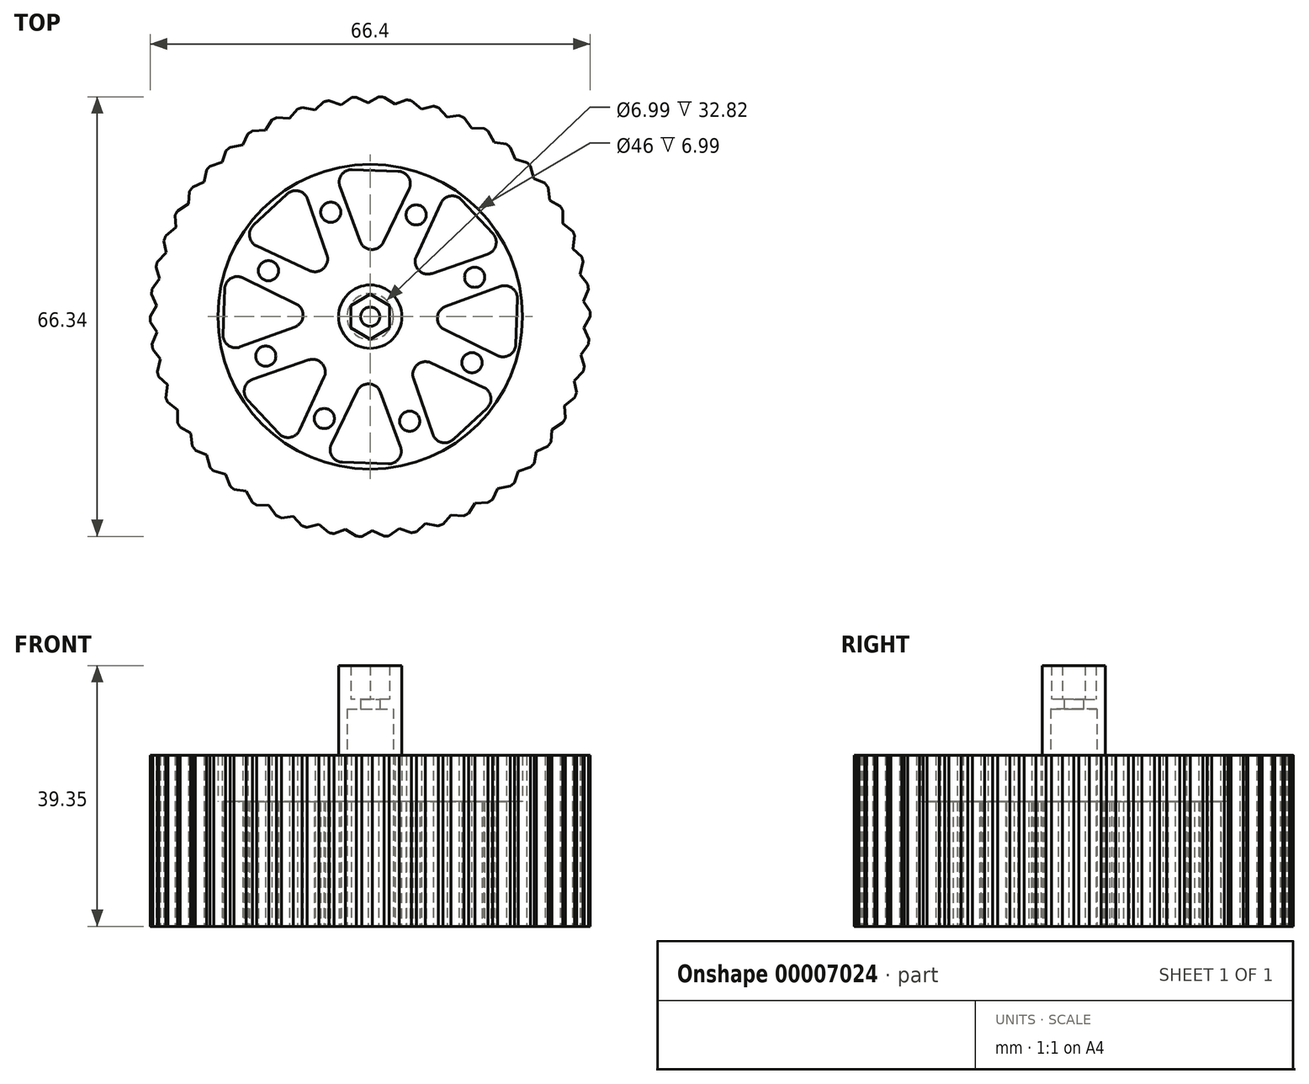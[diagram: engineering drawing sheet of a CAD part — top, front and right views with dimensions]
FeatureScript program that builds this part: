
annotation { "Feature Type Name" : "Feature", "Feature Type Description" : "" }
export const myFeature = defineFeature(function(context is Context, id is Id, definition is map)
    precondition{}
    {
        {
            var Q0;
            Q0=qCreatedBy(makeId("Top.planeOp"),FACE);
            var sketch = newSketch(context, id + "F0", { "sketchPlane" : qUnion([Q0])});
            skCircle(sketch, "E0", {"center": v(0, 0) * mm, "radius": 23 * mm});
            skSolve(sketch);
        }
        {
            var Q0;
            Q0 = qSketchRegion(id + "F0", true);
            extrude(context, id + "F1", {"entities" : qUnion([Q0]), "depth" : 3.8 * mm});
        }
        {
            var Q0;
            Q0=makeQuery(id+"F1.opExtrude","CAP_FACE",FACE,{"disambiguationData":[OSD([sQuery(id+"F0.wireOp",EDGE,"E0")])],"isStart":true});
            var sketch = newSketch(context, id + "F2", { "sketchPlane" : qUnion([Q0])});
            skLineSegment(sketch, "E1.0", {"start": v(4.22, -21.97) * mm, "end": v(-2.71, -22.22) * mm});
            skLineSegment(sketch, "E1.1", {"start": v(-4.57, -19.66) * mm, "end": v(-1.54, -11.39) * mm});
            skLineSegment(sketch, "E1.2", {"start": v(1.96, -11.2) * mm, "end": v(5.87, -19.23) * mm});
            skPoint(sketch, "E1.0.midPoint", {"position": v(0.8, -22.1) * mm});
            skLineSegment(sketch, "E2.1.0", {"start": v(10.67, -17.13) * mm, "end": v(6.96, -9.14) * mm});
            skLineSegment(sketch, "E2.1.1", {"start": v(9.31, -6.54) * mm, "end": v(17.75, -9.45) * mm});
            skLineSegment(sketch, "E2.1.2", {"start": v(18.52, -12.55) * mm, "end": v(13.8, -17.63) * mm});
            skLineSegment(sketch, "E2.2.0", {"start": v(19.66, -4.57) * mm, "end": v(11.39, -1.54) * mm});
            skLineSegment(sketch, "E2.2.1", {"start": v(11.2, 1.96) * mm, "end": v(19.23, 5.87) * mm});
            skLineSegment(sketch, "E2.2.2", {"start": v(21.97, 4.22) * mm, "end": v(22.22, -2.71) * mm});
            skLineSegment(sketch, "E2.3.0", {"start": v(17.13, 10.67) * mm, "end": v(9.14, 6.96) * mm});
            skLineSegment(sketch, "E2.3.1", {"start": v(6.54, 9.31) * mm, "end": v(9.45, 17.75) * mm});
            skLineSegment(sketch, "E2.3.2", {"start": v(12.55, 18.52) * mm, "end": v(17.63, 13.8) * mm});
            skLineSegment(sketch, "E2.4.0", {"start": v(4.57, 19.66) * mm, "end": v(1.54, 11.39) * mm});
            skLineSegment(sketch, "E2.4.1", {"start": v(-1.96, 11.2) * mm, "end": v(-5.87, 19.23) * mm});
            skLineSegment(sketch, "E2.4.2", {"start": v(-4.22, 21.97) * mm, "end": v(2.71, 22.22) * mm});
            skLineSegment(sketch, "E2.5.0", {"start": v(-10.67, 17.13) * mm, "end": v(-6.96, 9.14) * mm});
            skLineSegment(sketch, "E2.5.1", {"start": v(-9.31, 6.54) * mm, "end": v(-17.75, 9.45) * mm});
            skLineSegment(sketch, "E2.5.2", {"start": v(-18.52, 12.55) * mm, "end": v(-13.8, 17.63) * mm});
            skLineSegment(sketch, "E2.6.0", {"start": v(-19.66, 4.57) * mm, "end": v(-11.39, 1.54) * mm});
            skLineSegment(sketch, "E2.6.1", {"start": v(-11.2, -1.96) * mm, "end": v(-19.23, -5.87) * mm});
            skLineSegment(sketch, "E2.6.2", {"start": v(-21.97, -4.22) * mm, "end": v(-22.22, 2.71) * mm});
            skLineSegment(sketch, "E2.7.0", {"start": v(-17.13, -10.67) * mm, "end": v(-9.14, -6.96) * mm});
            skLineSegment(sketch, "E2.7.1", {"start": v(-6.54, -9.31) * mm, "end": v(-9.45, -17.75) * mm});
            skLineSegment(sketch, "E2.7.2", {"start": v(-12.55, -18.52) * mm, "end": v(-17.63, -13.8) * mm});
            skPoint(sketch, "E2.center", {"position": v(0, 0) * mm});
            skLineSegment(sketch, "E3", {"start": v(0.8, -22.1) * mm, "end": v(0, -7.18) * mm, "construction": true});
            skLineSegment(sketch, "E4", {"start": v(-11.86, 19.7) * mm, "end": v(-7.15, 21.86) * mm, "construction": true});
            skLineSegment(sketch, "E5", {"start": v(0, 7.18) * mm, "end": v(0, 0) * mm, "construction": true});
            skLineSegment(sketch, "E6", {"start": v(-7.18, 0) * mm, "end": v(7.18, 0) * mm, "construction": true});
            skPoint(sketch, "E7.visualSharp", {"position": v(-19.7, -11.86) * mm});
            skArc(sketch, "E7.filletArc", {"start": v(-17.13, -10.67) * mm, "mid": v(-18.21, -12.1) * mm, "end": v(-17.63, -13.8) * mm});
            skPoint(sketch, "E8.visualSharp", {"position": v(-10.4, -20.51) * mm});
            skArc(sketch, "E8.filletArc", {"start": v(-12.55, -18.52) * mm, "mid": v(-10.79, -18.97) * mm, "end": v(-9.45, -17.75) * mm});
            skPoint(sketch, "E9.visualSharp", {"position": v(-5.08, -5.08) * mm});
            skArc(sketch, "E9.filletArc", {"start": v(-6.54, -9.31) * mm, "mid": v(-7.06, -7.28) * mm, "end": v(-9.14, -6.96) * mm});
            skPoint(sketch, "E10.visualSharp", {"position": v(-7.18, 0) * mm});
            skArc(sketch, "E10.filletArc", {"start": v(-11.2, -1.96) * mm, "mid": v(-10.14, -0.15) * mm, "end": v(-11.39, 1.54) * mm});
            skPoint(sketch, "E11.visualSharp", {"position": v(-22.32, 5.55) * mm});
            skArc(sketch, "E11.filletArc", {"start": v(-19.66, 4.57) * mm, "mid": v(-21.43, 4.32) * mm, "end": v(-22.22, 2.71) * mm});
            skPoint(sketch, "E12.visualSharp", {"position": v(-21.86, -7.15) * mm});
            skArc(sketch, "E12.filletArc", {"start": v(-21.97, -4.22) * mm, "mid": v(-21.04, -5.79) * mm, "end": v(-19.23, -5.87) * mm});
            skPoint(sketch, "E13.visualSharp", {"position": v(-20.51, 10.4) * mm});
            skArc(sketch, "E13.filletArc", {"start": v(-18.52, 12.55) * mm, "mid": v(-18.97, 10.79) * mm, "end": v(-17.75, 9.45) * mm});
            skPoint(sketch, "E14.visualSharp", {"position": v(-11.86, 19.7) * mm});
            skArc(sketch, "E14.filletArc", {"start": v(-10.67, 17.13) * mm, "mid": v(-12.1, 18.21) * mm, "end": v(-13.8, 17.63) * mm});
            skPoint(sketch, "E15.visualSharp", {"position": v(-5.08, 5.08) * mm});
            skArc(sketch, "E15.filletArc", {"start": v(-9.31, 6.54) * mm, "mid": v(-7.28, 7.06) * mm, "end": v(-6.96, 9.14) * mm});
            skPoint(sketch, "E16.visualSharp", {"position": v(0, 7.18) * mm});
            skArc(sketch, "E16.filletArc", {"start": v(-1.96, 11.2) * mm, "mid": v(-0.15, 10.14) * mm, "end": v(1.54, 11.39) * mm});
            skPoint(sketch, "E17.visualSharp", {"position": v(-7.15, 21.86) * mm});
            skArc(sketch, "E17.filletArc", {"start": v(-4.22, 21.97) * mm, "mid": v(-5.79, 21.04) * mm, "end": v(-5.87, 19.23) * mm});
            skPoint(sketch, "E18.visualSharp", {"position": v(5.55, 22.32) * mm});
            skArc(sketch, "E18.filletArc", {"start": v(4.57, 19.66) * mm, "mid": v(4.32, 21.43) * mm, "end": v(2.71, 22.22) * mm});
            skPoint(sketch, "E19.visualSharp", {"position": v(5.08, 5.08) * mm});
            skArc(sketch, "E19.filletArc", {"start": v(6.54, 9.31) * mm, "mid": v(7.06, 7.28) * mm, "end": v(9.14, 6.96) * mm});
            skPoint(sketch, "E20.visualSharp", {"position": v(10.4, 20.51) * mm});
            skArc(sketch, "E20.filletArc", {"start": v(12.55, 18.52) * mm, "mid": v(10.79, 18.97) * mm, "end": v(9.45, 17.75) * mm});
            skPoint(sketch, "E21.visualSharp", {"position": v(19.7, 11.86) * mm});
            skArc(sketch, "E21.filletArc", {"start": v(17.13, 10.67) * mm, "mid": v(18.21, 12.1) * mm, "end": v(17.63, 13.8) * mm});
            skPoint(sketch, "E22.visualSharp", {"position": v(21.86, 7.15) * mm});
            skArc(sketch, "E22.filletArc", {"start": v(21.97, 4.22) * mm, "mid": v(21.04, 5.79) * mm, "end": v(19.23, 5.87) * mm});
            skPoint(sketch, "E23.visualSharp", {"position": v(7.18, 0) * mm});
            skArc(sketch, "E23.filletArc", {"start": v(11.2, 1.96) * mm, "mid": v(10.14, 0.15) * mm, "end": v(11.39, -1.54) * mm});
            skPoint(sketch, "E24.visualSharp", {"position": v(22.32, -5.55) * mm});
            skArc(sketch, "E24.filletArc", {"start": v(19.66, -4.57) * mm, "mid": v(21.43, -4.32) * mm, "end": v(22.22, -2.71) * mm});
            skPoint(sketch, "E25.visualSharp", {"position": v(11.86, -19.7) * mm});
            skArc(sketch, "E25.filletArc", {"start": v(10.67, -17.13) * mm, "mid": v(12.1, -18.21) * mm, "end": v(13.8, -17.63) * mm});
            skPoint(sketch, "E26.visualSharp", {"position": v(5.08, -5.08) * mm});
            skArc(sketch, "E26.filletArc", {"start": v(9.31, -6.54) * mm, "mid": v(7.28, -7.06) * mm, "end": v(6.96, -9.14) * mm});
            skPoint(sketch, "E27.visualSharp", {"position": v(20.51, -10.4) * mm});
            skArc(sketch, "E27.filletArc", {"start": v(18.52, -12.55) * mm, "mid": v(18.97, -10.79) * mm, "end": v(17.75, -9.45) * mm});
            skPoint(sketch, "E28.visualSharp", {"position": v(0, -7.18) * mm});
            skArc(sketch, "E28.filletArc", {"start": v(1.96, -11.2) * mm, "mid": v(0.15, -10.14) * mm, "end": v(-1.54, -11.39) * mm});
            skPoint(sketch, "E29.visualSharp", {"position": v(-5.55, -22.32) * mm});
            skArc(sketch, "E29.filletArc", {"start": v(-4.57, -19.66) * mm, "mid": v(-4.32, -21.43) * mm, "end": v(-2.71, -22.22) * mm});
            skPoint(sketch, "E30.visualSharp", {"position": v(7.15, -21.86) * mm});
            skArc(sketch, "E30.filletArc", {"start": v(4.22, -21.97) * mm, "mid": v(5.79, -21.04) * mm, "end": v(5.87, -19.23) * mm});
            skSolve(sketch);
        }
        {
            var Q0;
            {var subQ11=sQuery(id+"F2.wireOp",EDGE,"E1.1");Q0=makeQuery(id+"F2.imprint","IMPRINT",FACE,{"disambiguationData":[TD([[makeQuery(id+"F2.imprint","IMPRINT",EDGE,{"derivedFrom":subQ11}),1.0]])]});}
            var sketch = newSketch(context, id + "F3", { "sketchPlane" : qUnion([Q0])});
            skCircle(sketch, "E31", {"center": v(0, 0) * mm, "radius": 4.79 * mm});
            skSolve(sketch);
        }
        {
            var Q0;
            Q0 = qSketchRegion(id + "F3", true);
            extrude(context, id + "F4", {"entities" : qUnion([Q0]), "operationType" : NewBodyOperationType.ADD, "oppositeDirection" : true, "depth" : 14.55 * mm});
        }
        {
            var Q0;
            Q0=makeQuery(id+"F3.imprint","IMPRINT",FACE,{"disambiguationData":[TD([[makeQuery(id+"F3.imprint","IMPRINT",EDGE,{"derivedFrom":sQuery(id+"F3.wireOp",EDGE,"E31")}),1.0]])]});
            var sketch = newSketch(context, id + "F5", { "sketchPlane" : qUnion([Q0])});
            skCircle(sketch, "E32", {"center": v(0, 0) * mm, "radius": 3.5 * mm});
            skSolve(sketch);
        }
        {
            var Q0;
            Q0 = qSketchRegion(id + "F5", true);
            extrude(context, id + "F6", {"entities" : qUnion([Q0]), "operationType" : NewBodyOperationType.REMOVE, "oppositeDirection" : true, "depth" : 7.62 * mm});
        }
        {
            var Q0;
            Q0=makeQuery(id+"F4.opExtrude","CAP_FACE",FACE,{"disambiguationData":[OSD([sQuery(id+"F3.wireOp",EDGE,"E31")])],"isStart":false});
            var sketch = newSketch(context, id + "F7", { "sketchPlane" : qUnion([Q0])});
            skCircle(sketch, "E33.cCircle", {"center": v(0, 0) * mm, "radius": 2.93 * mm, "construction": true});
            skLineSegment(sketch, "E33.0", {"start": v(2.93, 1.69) * mm, "end": v(2.93, -1.69) * mm});
            skLineSegment(sketch, "E33.1", {"start": v(2.93, -1.69) * mm, "end": v(0, -3.38) * mm});
            skLineSegment(sketch, "E33.2", {"start": v(0, -3.38) * mm, "end": v(-2.93, -1.69) * mm});
            skLineSegment(sketch, "E33.3", {"start": v(-2.93, -1.69) * mm, "end": v(-2.93, 1.69) * mm});
            skLineSegment(sketch, "E33.4", {"start": v(-2.93, 1.69) * mm, "end": v(0, 3.38) * mm});
            skLineSegment(sketch, "E33.5", {"start": v(0, 3.38) * mm, "end": v(2.93, 1.69) * mm});
            skPoint(sketch, "E33.0.midPoint", {"position": v(2.93, 0) * mm});
            skSolve(sketch);
        }
        {
            var Q0;
            Q0=makeQuery(id+"F7.imprint","IMPRINT",FACE,{"disambiguationData":[TD([[makeQuery(id+"F7.imprint","IMPRINT",EDGE,{"derivedFrom":sQuery(id+"F7.wireOp",EDGE,"E33.0")}),-1.0]])]});
            extrude(context, id + "F8", {"entities" : qUnion([Q0]), "operationType" : NewBodyOperationType.REMOVE, "oppositeDirection" : true, "depth" : 5.08 * mm});
        }
        {
            var Q0;
            {var subQ11=sQuery(id+"F2.wireOp",EDGE,"E1.1");Q0=makeQuery(id+"F2.imprint","IMPRINT",FACE,{"disambiguationData":[TD([[makeQuery(id+"F2.imprint","IMPRINT",EDGE,{"derivedFrom":subQ11}),1.0]])]});}
            var sketch = newSketch(context, id + "F9", { "sketchPlane" : qUnion([Q0])});
            skCircle(sketch, "E34", {"center": v(0, 0) * mm, "radius": 1.45 * mm});
            skSolve(sketch);
        }
        {
            var Q0;
            Q0 = qSketchRegion(id + "F9", true);
            extrude(context, id + "F10", {"entities" : qUnion([Q0]), "operationType" : NewBodyOperationType.REMOVE, "oppositeDirection" : true, "depth" : 25.4 * mm});
        }
        {
            var Q0;
            {var subQ11=sQuery(id+"F2.wireOp",EDGE,"E1.1");Q0=makeQuery(id+"F2.imprint","IMPRINT",FACE,{"disambiguationData":[TD([[makeQuery(id+"F2.imprint","IMPRINT",EDGE,{"derivedFrom":subQ11}),1.0]])]});}
            var sketch = newSketch(context, id + "F11", { "sketchPlane" : qUnion([Q0])});
            skLineSegment(sketch, "E35", {"start": v(8.77, 15.77) * mm, "end": v(3.15, 15.77) * mm, "construction": true});
            skCircle(sketch, "E36", {"center": v(5.96, 15.77) * mm, "radius": 1.52 * mm});
            skCircle(sketch, "E37.1.0", {"center": v(-6.94, 15.37) * mm, "radius": 1.52 * mm});
            skCircle(sketch, "E37.2.0", {"center": v(-15.77, 5.96) * mm, "radius": 1.52 * mm});
            skCircle(sketch, "E37.3.0", {"center": v(-15.37, -6.94) * mm, "radius": 1.52 * mm});
            skCircle(sketch, "E37.4.0", {"center": v(-5.96, -15.77) * mm, "radius": 1.52 * mm});
            skCircle(sketch, "E37.5.0", {"center": v(6.94, -15.37) * mm, "radius": 1.52 * mm});
            skCircle(sketch, "E37.6.0", {"center": v(15.77, -5.96) * mm, "radius": 1.52 * mm});
            skCircle(sketch, "E37.7.0", {"center": v(15.37, 6.94) * mm, "radius": 1.52 * mm});
            skPoint(sketch, "E37.center", {"position": v(0, 0) * mm});
            skSolve(sketch);
        }
        {
            var Q0;
            Q0 = qSketchRegion(id + "F11", true);
            extrude(context, id + "F12", {"entities" : qUnion([Q0]), "operationType" : NewBodyOperationType.REMOVE, "oppositeDirection" : true, "depth" : 12.7 * mm});
        }
        {
            var Q0;
            Q0=makeQuery(id+"F3.imprint","IMPRINT",FACE,{"disambiguationData":[TD([[makeQuery(id+"F3.imprint","IMPRINT",EDGE,{"derivedFrom":sQuery(id+"F3.wireOp",EDGE,"E31")}),-1.0]])]});
            var sketch = newSketch(context, id + "F13", { "sketchPlane" : qUnion([Q0])});
            skCircle(sketch, "E38", {"center": v(0, 0) * mm, "radius": 33.2 * mm});
            skCircle(sketch, "E39", {"center": v(0, 0) * mm, "radius": 21.9 * mm});
            skCircle(sketch, "E40.0", {"center": v(0, 0) * mm, "radius": 23 * mm});
            skSolve(sketch);
        }
        {
            var Q0;
            Q0 = qSketchRegion(id + "F2", true);
            extrude(context, id + "F14", {"entities" : qUnion([Q0]), "operationType" : NewBodyOperationType.REMOVE, "oppositeDirection" : true, "depth" : 12.7 * mm, "offsetDistance" : 25 * mm});
        }
        {
            var Q0;
            Q0=makeQuery(id+"F13.imprint","IMPRINT",FACE,{"disambiguationData":[TD([[makeQuery(id+"F13.imprint","IMPRINT",EDGE,{"derivedFrom":sQuery(id+"F13.wireOp",EDGE,"E38")}),1.0]])]});
            extrude(context, id + "F15", {"entities" : qUnion([Q0]), "operationType" : NewBodyOperationType.ADD, "oppositeDirection" : true, "depth" : 18 * mm, "offsetDistance" : 25 * mm});
        }
        {
            var Q0;
            Q0=makeQuery(id+"F4.opExtrude","CAP_FACE",FACE,{"disambiguationData":[OSD([sQuery(id+"F3.wireOp",EDGE,"E31")])],"isStart":false});
            extrude(context, id + "F16", {"entities" : qUnion([Q0]), "operationType" : NewBodyOperationType.ADD, "depth" : 17 * mm, "offsetDistance" : 25 * mm});
        }
        {
            var Q0;
            Q0=makeQuery(id+"F8.boolean.opBoolean","COPY",FACE,{"derivedFrom":makeQuery(id+"F8.opExtrude","CAP_FACE",FACE,{"disambiguationData":[OSD([sQuery(id+"F7.wireOp",EDGE,"E33.0"),sQuery(id+"F7.wireOp",EDGE,"E33.1"),sQuery(id+"F7.wireOp",EDGE,"E33.2"),sQuery(id+"F7.wireOp",EDGE,"E33.3"),sQuery(id+"F7.wireOp",EDGE,"E33.4"),sQuery(id+"F7.wireOp",EDGE,"E33.5")])],"isStart":false})});
            extrude(context, id + "F17", {"entities" : qUnion([Q0]), "operationType" : NewBodyOperationType.ADD, "depth" : 17 * mm, "offsetDistance" : 25 * mm});
        }
        {
            var Q0;
            Q0=makeQuery(id+"F6.boolean.opBoolean","COPY",FACE,{"derivedFrom":makeQuery(id+"F6.opExtrude","CAP_FACE",FACE,{"disambiguationData":[OSD([sQuery(id+"F5.wireOp",EDGE,"E32")])],"isStart":false})});
            extrude(context, id + "F18", {"entities" : qUnion([Q0]), "operationType" : NewBodyOperationType.REMOVE, "oppositeDirection" : true, "depth" : 17.4 * mm, "offsetDistance" : 25 * mm});
        }
        {
            var Q0;
            Q0=makeQuery(id+"F1.opExtrude","CAP_FACE",FACE,{"disambiguationData":[OSD([sQuery(id+"F0.wireOp",EDGE,"E0")])],"isStart":false});
            extrude(context, id + "F19", {"entities" : qUnion([Q0]), "operationType" : NewBodyOperationType.ADD, "depth" : 11.5 * mm, "offsetDistance" : 25 * mm});
        }
        {
            var Q0;
            Q0=makeQuery(id+"F15.boolean.opBoolean","MERGE",FACE,{"derivedFrom":[makeQuery(id+"F1.opExtrude","CAP_FACE",FACE,{"disambiguationData":[OSD([sQuery(id+"F0.wireOp",EDGE,"E0")])],"isStart":true}),makeQuery(id+"F15.opExtrude","CAP_FACE",FACE,{"disambiguationData":[OSD([sQuery(id+"F13.wireOp",EDGE,"E38"),sQuery(id+"F13.wireOp",EDGE,"E40.0")])],"isStart":true})]});
            var sketch = newSketch(context, id + "F20", { "sketchPlane" : qUnion([Q0])});
            skLineSegment(sketch, "E41", {"start": v(33.03, 3.38) * mm, "end": v(32.25, 1.7) * mm});
            skLineSegment(sketch, "E42", {"start": v(32.25, 1.7) * mm, "end": v(33.2, 0) * mm});
            skArc(sketch, "E43.0", {"start": v(33.2, 0) * mm, "mid": v(33.16, 1.7) * mm, "end": v(33.03, 3.38) * mm});
            skLineSegment(sketch, "E44.1.0", {"start": v(31.78, 5.74) * mm, "end": v(32.94, 4.16) * mm});
            skLineSegment(sketch, "E44.1.1", {"start": v(32.34, 7.49) * mm, "end": v(31.78, 5.74) * mm});
            skArc(sketch, "E44.1.2", {"start": v(32.94, 4.16) * mm, "mid": v(32.68, 5.83) * mm, "end": v(32.34, 7.49) * mm});
            skLineSegment(sketch, "E44.2.0", {"start": v(30.81, 9.68) * mm, "end": v(32.16, 8.26) * mm});
            skLineSegment(sketch, "E44.2.1", {"start": v(31.15, 11.48) * mm, "end": v(30.81, 9.68) * mm});
            skArc(sketch, "E44.2.2", {"start": v(32.16, 8.26) * mm, "mid": v(31.7, 9.88) * mm, "end": v(31.15, 11.48) * mm});
            skLineSegment(sketch, "E44.3.0", {"start": v(29.36, 13.46) * mm, "end": v(30.87, 12.22) * mm});
            skLineSegment(sketch, "E44.3.1", {"start": v(29.47, 15.3) * mm, "end": v(29.36, 13.46) * mm});
            skArc(sketch, "E44.3.2", {"start": v(30.87, 12.22) * mm, "mid": v(30.2, 13.78) * mm, "end": v(29.47, 15.3) * mm});
            skLineSegment(sketch, "E44.4.0", {"start": v(27.44, 17.04) * mm, "end": v(29.1, 16) * mm});
            skLineSegment(sketch, "E44.4.1", {"start": v(27.32, 18.87) * mm, "end": v(27.44, 17.04) * mm});
            skArc(sketch, "E44.4.2", {"start": v(29.1, 16) * mm, "mid": v(28.24, 17.45) * mm, "end": v(27.32, 18.87) * mm});
            skLineSegment(sketch, "E44.5.0", {"start": v(25.09, 20.34) * mm, "end": v(26.86, 19.51) * mm});
            skLineSegment(sketch, "E44.5.1", {"start": v(24.73, 22.15) * mm, "end": v(25.09, 20.34) * mm});
            skArc(sketch, "E44.5.2", {"start": v(26.86, 19.51) * mm, "mid": v(25.83, 20.86) * mm, "end": v(24.73, 22.15) * mm});
            skLineSegment(sketch, "E44.6.0", {"start": v(22.34, 23.32) * mm, "end": v(24.2, 22.73) * mm});
            skLineSegment(sketch, "E44.6.1", {"start": v(21.76, 25.07) * mm, "end": v(22.34, 23.32) * mm});
            skArc(sketch, "E44.6.2", {"start": v(24.2, 22.73) * mm, "mid": v(23.01, 23.93) * mm, "end": v(21.76, 25.07) * mm});
            skLineSegment(sketch, "E44.7.0", {"start": v(19.24, 25.94) * mm, "end": v(21.16, 25.58) * mm});
            skLineSegment(sketch, "E44.7.1", {"start": v(18.45, 27.6) * mm, "end": v(19.24, 25.94) * mm});
            skArc(sketch, "E44.7.2", {"start": v(21.16, 25.58) * mm, "mid": v(19.83, 26.63) * mm, "end": v(18.45, 27.6) * mm});
            skLineSegment(sketch, "E44.8.0", {"start": v(15.84, 28.15) * mm, "end": v(17.79, 28.03) * mm});
            skLineSegment(sketch, "E44.8.1", {"start": v(14.85, 29.7) * mm, "end": v(15.84, 28.15) * mm});
            skArc(sketch, "E44.8.2", {"start": v(17.79, 28.03) * mm, "mid": v(16.34, 28.9) * mm, "end": v(14.85, 29.7) * mm});
            skLineSegment(sketch, "E44.9.0", {"start": v(12.19, 29.91) * mm, "end": v(14.14, 30.04) * mm});
            skLineSegment(sketch, "E44.9.1", {"start": v(11, 31.32) * mm, "end": v(12.19, 29.91) * mm});
            skArc(sketch, "E44.9.2", {"start": v(14.14, 30.04) * mm, "mid": v(12.59, 30.72) * mm, "end": v(11, 31.32) * mm});
            skLineSegment(sketch, "E44.10.0", {"start": v(8.34, 31.2) * mm, "end": v(10.26, 31.57) * mm});
            skLineSegment(sketch, "E44.10.1", {"start": v(7, 32.45) * mm, "end": v(8.34, 31.2) * mm});
            skArc(sketch, "E44.10.2", {"start": v(10.26, 31.57) * mm, "mid": v(8.64, 32.06) * mm, "end": v(7, 32.45) * mm});
            skLineSegment(sketch, "E44.11.0", {"start": v(4.36, 32) * mm, "end": v(6.22, 32.61) * mm});
            skLineSegment(sketch, "E44.11.1", {"start": v(2.87, 33.08) * mm, "end": v(4.36, 32) * mm});
            skArc(sketch, "E44.11.2", {"start": v(6.22, 32.61) * mm, "mid": v(4.55, 32.89) * mm, "end": v(2.87, 33.08) * mm});
            skLineSegment(sketch, "E44.12.0", {"start": v(0.32, 32.3) * mm, "end": v(2.08, 33.13) * mm});
            skLineSegment(sketch, "E44.12.1", {"start": v(-1.3, 33.17) * mm, "end": v(0.32, 32.3) * mm});
            skArc(sketch, "E44.12.2", {"start": v(2.08, 33.13) * mm, "mid": v(0.4, 33.2) * mm, "end": v(-1.3, 33.17) * mm});
            skLineSegment(sketch, "E44.13.0", {"start": v(-3.73, 32.08) * mm, "end": v(-2.08, 33.13) * mm});
            skLineSegment(sketch, "E44.13.1", {"start": v(-5.44, 32.75) * mm, "end": v(-3.73, 32.08) * mm});
            skArc(sketch, "E44.13.2", {"start": v(-2.08, 33.13) * mm, "mid": v(-3.77, 32.99) * mm, "end": v(-5.44, 32.75) * mm});
            skLineSegment(sketch, "E44.14.0", {"start": v(-7.72, 31.36) * mm, "end": v(-6.22, 32.61) * mm});
            skLineSegment(sketch, "E44.14.1", {"start": v(-9.5, 31.8) * mm, "end": v(-7.72, 31.36) * mm});
            skArc(sketch, "E44.14.2", {"start": v(-6.22, 32.61) * mm, "mid": v(-7.87, 32.25) * mm, "end": v(-9.5, 31.8) * mm});
            skLineSegment(sketch, "E44.15.0", {"start": v(-11.6, 30.15) * mm, "end": v(-10.26, 31.57) * mm});
            skLineSegment(sketch, "E44.15.1", {"start": v(-13.42, 30.37) * mm, "end": v(-11.6, 30.15) * mm});
            skArc(sketch, "E44.15.2", {"start": v(-10.26, 31.57) * mm, "mid": v(-11.85, 31.01) * mm, "end": v(-13.42, 30.37) * mm});
            skLineSegment(sketch, "E44.16.0", {"start": v(-15.28, 28.46) * mm, "end": v(-14.14, 30.04) * mm});
            skLineSegment(sketch, "E44.16.1", {"start": v(-17.12, 28.45) * mm, "end": v(-15.28, 28.46) * mm});
            skArc(sketch, "E44.16.2", {"start": v(-14.14, 30.04) * mm, "mid": v(-15.65, 29.28) * mm, "end": v(-17.12, 28.45) * mm});
            skLineSegment(sketch, "E44.17.0", {"start": v(-18.72, 26.32) * mm, "end": v(-17.79, 28.03) * mm});
            skLineSegment(sketch, "E44.17.1", {"start": v(-20.55, 26.08) * mm, "end": v(-18.72, 26.32) * mm});
            skArc(sketch, "E44.17.2", {"start": v(-17.79, 28.03) * mm, "mid": v(-19.2, 27.09) * mm, "end": v(-20.55, 26.08) * mm});
            skLineSegment(sketch, "E44.18.0", {"start": v(-21.88, 23.76) * mm, "end": v(-21.16, 25.58) * mm});
            skLineSegment(sketch, "E44.18.1", {"start": v(-23.65, 23.3) * mm, "end": v(-21.88, 23.76) * mm});
            skArc(sketch, "E44.18.2", {"start": v(-21.16, 25.58) * mm, "mid": v(-22.44, 24.47) * mm, "end": v(-23.65, 23.3) * mm});
            skLineSegment(sketch, "E44.19.0", {"start": v(-24.68, 20.83) * mm, "end": v(-24.2, 22.73) * mm});
            skLineSegment(sketch, "E44.19.1", {"start": v(-26.39, 20.15) * mm, "end": v(-24.68, 20.83) * mm});
            skArc(sketch, "E44.19.2", {"start": v(-24.2, 22.73) * mm, "mid": v(-25.33, 21.46) * mm, "end": v(-26.39, 20.15) * mm});
            skLineSegment(sketch, "E44.20.0", {"start": v(-27.1, 17.58) * mm, "end": v(-26.86, 19.51) * mm});
            skLineSegment(sketch, "E44.20.1", {"start": v(-28.7, 16.68) * mm, "end": v(-27.1, 17.58) * mm});
            skArc(sketch, "E44.20.2", {"start": v(-26.86, 19.51) * mm, "mid": v(-27.82, 18.12) * mm, "end": v(-28.7, 16.68) * mm});
            skLineSegment(sketch, "E44.21.0", {"start": v(-29.09, 14.04) * mm, "end": v(-29.1, 16) * mm});
            skLineSegment(sketch, "E44.21.1", {"start": v(-30.57, 12.95) * mm, "end": v(-29.09, 14.04) * mm});
            skArc(sketch, "E44.21.2", {"start": v(-29.1, 16) * mm, "mid": v(-29.87, 14.5) * mm, "end": v(-30.57, 12.95) * mm});
            skLineSegment(sketch, "E44.22.0", {"start": v(-30.62, 10.28) * mm, "end": v(-30.87, 12.22) * mm});
            skLineSegment(sketch, "E44.22.1", {"start": v(-31.95, 9.02) * mm, "end": v(-30.62, 10.28) * mm});
            skArc(sketch, "E44.22.2", {"start": v(-30.87, 12.22) * mm, "mid": v(-31.45, 10.63) * mm, "end": v(-31.95, 9.02) * mm});
            skLineSegment(sketch, "E44.23.0", {"start": v(-31.66, 6.37) * mm, "end": v(-32.16, 8.26) * mm});
            skLineSegment(sketch, "E44.23.1", {"start": v(-32.83, 4.94) * mm, "end": v(-31.66, 6.37) * mm});
            skArc(sketch, "E44.23.2", {"start": v(-32.16, 8.26) * mm, "mid": v(-32.54, 6.6) * mm, "end": v(-32.83, 4.94) * mm});
            skLineSegment(sketch, "E44.24.0", {"start": v(-32.21, 2.35) * mm, "end": v(-32.94, 4.16) * mm});
            skLineSegment(sketch, "E44.24.1", {"start": v(-33.2, 0.79) * mm, "end": v(-32.21, 2.35) * mm});
            skArc(sketch, "E44.24.2", {"start": v(-32.94, 4.16) * mm, "mid": v(-33.1, 2.48) * mm, "end": v(-33.2, 0.79) * mm});
            skLineSegment(sketch, "E44.25.0", {"start": v(-32.25, -1.7) * mm, "end": v(-33.2, 0) * mm});
            skLineSegment(sketch, "E44.25.1", {"start": v(-33.03, -3.38) * mm, "end": v(-32.25, -1.7) * mm});
            skArc(sketch, "E44.25.2", {"start": v(-33.2, 0) * mm, "mid": v(-33.16, -1.7) * mm, "end": v(-33.03, -3.38) * mm});
            skLineSegment(sketch, "E44.26.0", {"start": v(-31.78, -5.74) * mm, "end": v(-32.94, -4.16) * mm});
            skLineSegment(sketch, "E44.26.1", {"start": v(-32.34, -7.49) * mm, "end": v(-31.78, -5.74) * mm});
            skArc(sketch, "E44.26.2", {"start": v(-32.94, -4.16) * mm, "mid": v(-32.68, -5.83) * mm, "end": v(-32.34, -7.49) * mm});
            skLineSegment(sketch, "E44.27.0", {"start": v(-30.81, -9.68) * mm, "end": v(-32.16, -8.26) * mm});
            skLineSegment(sketch, "E44.27.1", {"start": v(-31.15, -11.48) * mm, "end": v(-30.81, -9.68) * mm});
            skArc(sketch, "E44.27.2", {"start": v(-32.16, -8.26) * mm, "mid": v(-31.7, -9.88) * mm, "end": v(-31.15, -11.48) * mm});
            skLineSegment(sketch, "E44.28.0", {"start": v(-29.36, -13.46) * mm, "end": v(-30.87, -12.22) * mm});
            skLineSegment(sketch, "E44.28.1", {"start": v(-29.47, -15.3) * mm, "end": v(-29.36, -13.46) * mm});
            skArc(sketch, "E44.28.2", {"start": v(-30.87, -12.22) * mm, "mid": v(-30.2, -13.78) * mm, "end": v(-29.47, -15.3) * mm});
            skLineSegment(sketch, "E44.29.0", {"start": v(-27.44, -17.04) * mm, "end": v(-29.1, -16) * mm});
            skLineSegment(sketch, "E44.29.1", {"start": v(-27.32, -18.87) * mm, "end": v(-27.44, -17.04) * mm});
            skArc(sketch, "E44.29.2", {"start": v(-29.1, -16) * mm, "mid": v(-28.24, -17.45) * mm, "end": v(-27.32, -18.87) * mm});
            skLineSegment(sketch, "E44.30.0", {"start": v(-25.09, -20.34) * mm, "end": v(-26.86, -19.51) * mm});
            skLineSegment(sketch, "E44.30.1", {"start": v(-24.73, -22.15) * mm, "end": v(-25.09, -20.34) * mm});
            skArc(sketch, "E44.30.2", {"start": v(-26.86, -19.51) * mm, "mid": v(-25.83, -20.86) * mm, "end": v(-24.73, -22.15) * mm});
            skLineSegment(sketch, "E44.31.0", {"start": v(-22.34, -23.32) * mm, "end": v(-24.2, -22.73) * mm});
            skLineSegment(sketch, "E44.31.1", {"start": v(-21.76, -25.07) * mm, "end": v(-22.34, -23.32) * mm});
            skArc(sketch, "E44.31.2", {"start": v(-24.2, -22.73) * mm, "mid": v(-23.01, -23.93) * mm, "end": v(-21.76, -25.07) * mm});
            skLineSegment(sketch, "E44.32.0", {"start": v(-19.24, -25.94) * mm, "end": v(-21.16, -25.58) * mm});
            skLineSegment(sketch, "E44.32.1", {"start": v(-18.45, -27.6) * mm, "end": v(-19.24, -25.94) * mm});
            skArc(sketch, "E44.32.2", {"start": v(-21.16, -25.58) * mm, "mid": v(-19.83, -26.63) * mm, "end": v(-18.45, -27.6) * mm});
            skLineSegment(sketch, "E44.33.0", {"start": v(-15.84, -28.15) * mm, "end": v(-17.79, -28.03) * mm});
            skLineSegment(sketch, "E44.33.1", {"start": v(-14.85, -29.7) * mm, "end": v(-15.84, -28.15) * mm});
            skArc(sketch, "E44.33.2", {"start": v(-17.79, -28.03) * mm, "mid": v(-16.34, -28.9) * mm, "end": v(-14.85, -29.7) * mm});
            skLineSegment(sketch, "E44.34.0", {"start": v(-12.19, -29.91) * mm, "end": v(-14.14, -30.04) * mm});
            skLineSegment(sketch, "E44.34.1", {"start": v(-11, -31.32) * mm, "end": v(-12.19, -29.91) * mm});
            skArc(sketch, "E44.34.2", {"start": v(-14.14, -30.04) * mm, "mid": v(-12.59, -30.72) * mm, "end": v(-11, -31.32) * mm});
            skLineSegment(sketch, "E44.35.0", {"start": v(-8.34, -31.2) * mm, "end": v(-10.26, -31.57) * mm});
            skLineSegment(sketch, "E44.35.1", {"start": v(-7, -32.45) * mm, "end": v(-8.34, -31.2) * mm});
            skArc(sketch, "E44.35.2", {"start": v(-10.26, -31.57) * mm, "mid": v(-8.64, -32.06) * mm, "end": v(-7, -32.45) * mm});
            skLineSegment(sketch, "E44.36.0", {"start": v(-4.36, -32) * mm, "end": v(-6.22, -32.61) * mm});
            skLineSegment(sketch, "E44.36.1", {"start": v(-2.87, -33.08) * mm, "end": v(-4.36, -32) * mm});
            skArc(sketch, "E44.36.2", {"start": v(-6.22, -32.61) * mm, "mid": v(-4.55, -32.89) * mm, "end": v(-2.87, -33.08) * mm});
            skLineSegment(sketch, "E44.37.0", {"start": v(-0.32, -32.3) * mm, "end": v(-2.08, -33.13) * mm});
            skLineSegment(sketch, "E44.37.1", {"start": v(1.3, -33.17) * mm, "end": v(-0.32, -32.3) * mm});
            skArc(sketch, "E44.37.2", {"start": v(-2.08, -33.13) * mm, "mid": v(-0.4, -33.2) * mm, "end": v(1.3, -33.17) * mm});
            skLineSegment(sketch, "E44.38.0", {"start": v(3.73, -32.08) * mm, "end": v(2.08, -33.13) * mm});
            skLineSegment(sketch, "E44.38.1", {"start": v(5.44, -32.75) * mm, "end": v(3.73, -32.08) * mm});
            skArc(sketch, "E44.38.2", {"start": v(2.08, -33.13) * mm, "mid": v(3.77, -32.99) * mm, "end": v(5.44, -32.75) * mm});
            skLineSegment(sketch, "E44.39.0", {"start": v(7.72, -31.36) * mm, "end": v(6.22, -32.61) * mm});
            skLineSegment(sketch, "E44.39.1", {"start": v(9.5, -31.8) * mm, "end": v(7.72, -31.36) * mm});
            skArc(sketch, "E44.39.2", {"start": v(6.22, -32.61) * mm, "mid": v(7.87, -32.25) * mm, "end": v(9.5, -31.8) * mm});
            skLineSegment(sketch, "E44.40.0", {"start": v(11.6, -30.15) * mm, "end": v(10.26, -31.57) * mm});
            skLineSegment(sketch, "E44.40.1", {"start": v(13.42, -30.37) * mm, "end": v(11.6, -30.15) * mm});
            skArc(sketch, "E44.40.2", {"start": v(10.26, -31.57) * mm, "mid": v(11.85, -31.01) * mm, "end": v(13.42, -30.37) * mm});
            skLineSegment(sketch, "E44.41.0", {"start": v(15.28, -28.46) * mm, "end": v(14.14, -30.04) * mm});
            skLineSegment(sketch, "E44.41.1", {"start": v(17.12, -28.45) * mm, "end": v(15.28, -28.46) * mm});
            skArc(sketch, "E44.41.2", {"start": v(14.14, -30.04) * mm, "mid": v(15.65, -29.28) * mm, "end": v(17.12, -28.45) * mm});
            skLineSegment(sketch, "E44.42.0", {"start": v(18.72, -26.32) * mm, "end": v(17.79, -28.03) * mm});
            skLineSegment(sketch, "E44.42.1", {"start": v(20.55, -26.08) * mm, "end": v(18.72, -26.32) * mm});
            skArc(sketch, "E44.42.2", {"start": v(17.79, -28.03) * mm, "mid": v(19.2, -27.09) * mm, "end": v(20.55, -26.08) * mm});
            skLineSegment(sketch, "E44.43.0", {"start": v(21.88, -23.76) * mm, "end": v(21.16, -25.58) * mm});
            skLineSegment(sketch, "E44.43.1", {"start": v(23.65, -23.3) * mm, "end": v(21.88, -23.76) * mm});
            skArc(sketch, "E44.43.2", {"start": v(21.16, -25.58) * mm, "mid": v(22.44, -24.47) * mm, "end": v(23.65, -23.3) * mm});
            skLineSegment(sketch, "E44.44.0", {"start": v(24.68, -20.83) * mm, "end": v(24.2, -22.73) * mm});
            skLineSegment(sketch, "E44.44.1", {"start": v(26.39, -20.15) * mm, "end": v(24.68, -20.83) * mm});
            skArc(sketch, "E44.44.2", {"start": v(24.2, -22.73) * mm, "mid": v(25.33, -21.46) * mm, "end": v(26.39, -20.15) * mm});
            skLineSegment(sketch, "E44.45.0", {"start": v(27.1, -17.58) * mm, "end": v(26.86, -19.51) * mm});
            skLineSegment(sketch, "E44.45.1", {"start": v(28.7, -16.68) * mm, "end": v(27.1, -17.58) * mm});
            skArc(sketch, "E44.45.2", {"start": v(26.86, -19.51) * mm, "mid": v(27.82, -18.12) * mm, "end": v(28.7, -16.68) * mm});
            skLineSegment(sketch, "E44.46.0", {"start": v(29.09, -14.04) * mm, "end": v(29.1, -16) * mm});
            skLineSegment(sketch, "E44.46.1", {"start": v(30.57, -12.95) * mm, "end": v(29.09, -14.04) * mm});
            skArc(sketch, "E44.46.2", {"start": v(29.1, -16) * mm, "mid": v(29.87, -14.5) * mm, "end": v(30.57, -12.95) * mm});
            skLineSegment(sketch, "E44.47.0", {"start": v(30.62, -10.28) * mm, "end": v(30.87, -12.22) * mm});
            skLineSegment(sketch, "E44.47.1", {"start": v(31.95, -9.02) * mm, "end": v(30.62, -10.28) * mm});
            skArc(sketch, "E44.47.2", {"start": v(30.87, -12.22) * mm, "mid": v(31.45, -10.63) * mm, "end": v(31.95, -9.02) * mm});
            skLineSegment(sketch, "E44.48.0", {"start": v(31.66, -6.37) * mm, "end": v(32.16, -8.26) * mm});
            skLineSegment(sketch, "E44.48.1", {"start": v(32.83, -4.94) * mm, "end": v(31.66, -6.37) * mm});
            skArc(sketch, "E44.48.2", {"start": v(32.16, -8.26) * mm, "mid": v(32.54, -6.6) * mm, "end": v(32.83, -4.94) * mm});
            skLineSegment(sketch, "E44.49.0", {"start": v(32.21, -2.35) * mm, "end": v(32.94, -4.16) * mm});
            skLineSegment(sketch, "E44.49.1", {"start": v(33.2, -0.79) * mm, "end": v(32.21, -2.35) * mm});
            skArc(sketch, "E44.49.2", {"start": v(32.94, -4.16) * mm, "mid": v(33.1, -2.48) * mm, "end": v(33.2, -0.79) * mm});
            skSolve(sketch);
        }
        {
            var Q0;
            Q0 = qSketchRegion(id + "F20", true);
            extrude(context, id + "F21", {"entities" : qUnion([Q0]), "operationType" : NewBodyOperationType.REMOVE, "oppositeDirection" : true, "depth" : 25 * mm, "offsetDistance" : 25 * mm});
        }
        {
            var Q0;
            Q0=makeQuery(id+"F15.opExtrude","CAP_FACE",FACE,{"disambiguationData":[OSD([sQuery(id+"F13.wireOp",EDGE,"E38"),sQuery(id+"F13.wireOp",EDGE,"E40.0")])],"isStart":false});
            var Q1;
            Q1=makeQuery(id+"F17.opExtrude","CAP_FACE",FACE,{"disambiguationData":[OSD([sQuery(id+"F7.wireOp",EDGE,"E33.0"),sQuery(id+"F7.wireOp",EDGE,"E33.1"),sQuery(id+"F7.wireOp",EDGE,"E33.2"),sQuery(id+"F7.wireOp",EDGE,"E33.3"),sQuery(id+"F7.wireOp",EDGE,"E33.4"),sQuery(id+"F7.wireOp",EDGE,"E33.5")])],"isStart":false});
            var Q2;
            Q2=makeQuery(id+"F16.opExtrude","CAP_FACE",FACE,{"disambiguationData":[OSD([sQuery(id+"F3.wireOp",EDGE,"E31")])],"isStart":false});
            extrude(context, id + "F22", {"entities" : qUnion([Q0, Q1, Q2]), "operationType" : NewBodyOperationType.ADD, "depth" : 7.8 * mm, "offsetDistance" : 25 * mm});
        }
        {
            var Q0;
            Q0=makeQuery(id+"F18.boolean.opBoolean","COPY",FACE,{"derivedFrom":makeQuery(id+"F18.opExtrude","CAP_FACE",FACE,{"disambiguationData":[OSD([sQuery(id+"F5.wireOp",EDGE,"E32")])],"isStart":false})});
            extrude(context, id + "F23", {"entities" : qUnion([Q0]), "operationType" : NewBodyOperationType.REMOVE, "oppositeDirection" : true, "depth" : 7.8 * mm, "offsetDistance" : 25 * mm});
        }
        {
            var Q0;
            Q0=makeQuery(id+"F19.opExtrude","CAP_FACE",FACE,{"disambiguationData":[OSD([sQuery(id+"F0.wireOp",EDGE,"E0")])],"isStart":false});
            extrude(context, id + "F24", {"entities" : qUnion([Q0]), "operationType" : NewBodyOperationType.ADD, "depth" : 3.5 * mm, "offsetDistance" : 25 * mm});
        }
    });
